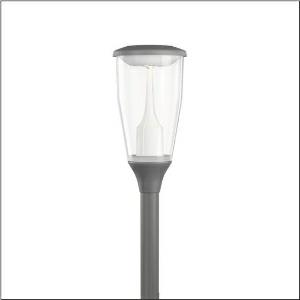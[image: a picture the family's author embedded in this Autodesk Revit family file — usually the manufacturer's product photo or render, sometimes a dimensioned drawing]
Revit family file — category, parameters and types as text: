
# Revit family: dl_11_iq___p1_0a_5xa5575ff14h000022_b904
name_source: partatom
category: Lighting Fixtures
units: mm (PartAtom-declared; Revit-internal decimal feet)

## family parameters
Cut with Voids When Loaded = No
Host = Face
Light Source = No
Part Type = Normal
Room Calculation Point = No
Round Connector Dimension = Use Diameter
Shared = No

## types (1)
- --- (1 x LED, 1530 lm, 10.5 W, 3000K)
    Apparent Load = 11 VA
    CIE Flux Codes = 34 63 91 95 100
    Color Rendering = 70
    Color Temperature = 3000K
    Default Elevation = 1800 mm
    Description = DL 11 iQ, mast luminaire, Module 540 iQ-SR, primary light control with 3 zone facetted reflector, of plastic, silver coated, highly specular, structured, primary optical cover: cover, of PMMA, transparent, light distribution: P1.0a, light emission: direct distribution, primary light characteristic: asymmetric, installation type: post-top, LED, High Power LED, rated luminous flux: 1.560lm, luminous efficacy: 149lm/W, light colour: 730, colour temperature: 3000K, control gear: iQ Street-Remote, control: Street-Remote, Auto-Match, Temp-Guard, Lumen-Switch, Night-Set, Smart-Wire, Light-Fading, Desk-Remote (wireless, voltage-free reading and setting of iQ features in the workshop via application-optimized NFC function/RFID function), optimised constant luminous flux control (CLO 2.0), mains connection: 220..240V, AC, 50/60Hz, connection cable pre-assembled, cable length: 5,5m, wiring characteristics: H07RN-F, 5-core, 1.5mm², start of lifetime: 10W, end of service life: 11W, reduction: 5W, luminaire housing, upper part, of diecast aluminium, coated, SITECO metallic grey (DB 702S), spigot size: 76mm (post-top), mounting height: 3..5m, post-top mast mounting element, of diecast aluminium, coated, SITECO metallic grey (DB 702S), Module 540 iQ-SR, traffic white (RAL 9016), equipment: standard, protection rating (complete): IP66, insulation class (complete): insulation class II (safety insulation), certification: CE, ENEC, ENEC+, VDE, impact resistance: IK07, packaging unit: 1 piece

Light Distribution: P1.0a
    Height = 665 mm
    Lamp = 1 x LED
    Lamp Light Flux = 1530 lm
    Lamp Power = 10.5 W
    Lamp count = 1
    Length = 334 mm
    Luminous efficacy = 146 lm/W
    Manufacturer = Siteco
    ModVariant = No
    Model = 5XA5575FF14H000022
    Number of Poles = 1
    OnlyDefault = Yes
    Power Factor = 1
    Product Name = DL 11 iQ | P1.0a
    Product group = mast luminaire | pylon top
    ProductGroupID = 6100
    Protection Class = Protection class II
    Protection Degree = IP 66
    RLX_Detail_Level = 1
    RLX_Emergency_Light_Flux = 0 lm
    RLX_Emergency_Type = 0
    RLX_Emergency_Type_DB = No
    RlxData = <blob elided: 103601 chars, md5=e3456b9e>
    Socket = socket
    Standby Power = 0 W
    System Light Flux = 1530 lm
    System Power = 11 W
    Type Comments = factory setting: luminous flux: 100 % | dim-lin: 254 | 419 mA
    Type Image = l_1258354.jpg
    URL = http://relux.com
    VarID = @adj_095615
    Voltage = 0 V
    Weight = 0.00 kg
    Width = 0 mm  [stored 0 ft]

note: [stored X ft] marks values corroborated as IEEE doubles in the binary element streams (Revit-internal decimal feet)

## geometry (parser evidence)
native form markers: Blend x4, Sweep x12
no freeform markers — native parametric forms only
